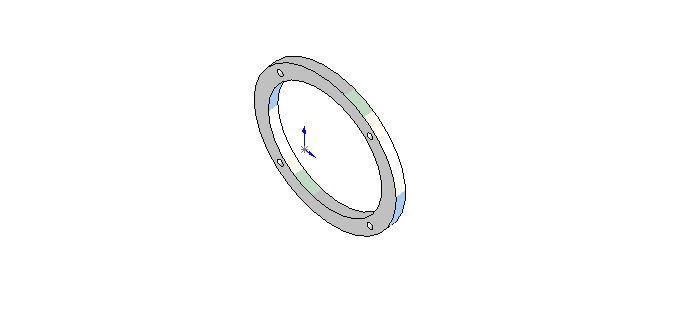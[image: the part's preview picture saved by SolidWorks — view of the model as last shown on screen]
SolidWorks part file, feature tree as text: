
SOLIDWORKS PART (.sldprt)
format: sldprt  version: not decoded by parser v0  size: 283,648 bytes
history: native  units: mm
features: sketch x4, plane x3, extrude x1 + 1 further entry (+7 scaffold rows collapsed)
feature tree (16):
  scaffold x7  (default folders/planes/origin — collapsed)
  "Corps de surface"
  plane  "Face"
  plane  "Dessus"
  plane  "Droite"
  sketch  "Esquisse1"  dims[c1.D1=4.8mm c1.D2=4.8mm c1.D7=4.8mm c1.D8=4.8mm c1.D17=~42.860884mm c1.D18=~42.860884mm c1.D3=32.0mm c1.D4=4.8mm c1.D5=8.0mm c1.D6=8.0mm c2.D7=4.8mm c2.D4=4.0mm c2.D5=5.6mm c2.D6=48.0mm c2.D9=32.0mm c2.D10=4.0mm c2.D11=5.6mm c2.D12=48.0mm c2.D13=28.8mm c2.D14=8.0mm c2.D15=8.0mm c2.D16=16.0mm c2.D18=48.0mm c3.D16=16.0mm c3.D17=8.0mm c3.D18=8.0mm c3.D19=4.0mm c3.D20=4.0mm c3.D21=24.0mm c3.D22=25.0mm c3.D13=28.8mm c3.D3=64.0mm c3.D12=8.0mm c4.D17=8.0mm c4.D9=8.0mm c4.D12=64.0mm c5.D17=48.0mm c5.D18=8.0mm c5.D9=32.0mm c6.D17=16.0mm c6.D18=16.0mm]
  sketch  "Esquisse5"  dims[c1.D12=2.1mm c1.D16=2.1mm c1.D1=8.0mm c1.D2=8.0mm c1.D3=4.0mm c1.D4=4.0mm c1.D5=25.0mm c1.D6=24.0mm c1.D7=12.5mm c1.D8=9.6mm c1.D9=5.5mm c1.D10=20.8mm c1.D11=10.4mm c1.D13=9.5mm c1.D14=2.0mm c1.D15=12.5mm c2.D16=~5.972653mm]
  sketch  "Esquisse6"  dims[D1=75.0mm D5=5.0mm D6=5.0mm D7=5.0mm D8=5.0mm D9=2.1mm D10=2.1mm D11=2.1mm D12=2.1mm D2=2.5mm D3=2.5mm D4=2.0mm]
  sketch  "Esquisse7"  dims[c1.D1=75.0mm c1.D2=60.0mm c1.D3=3.1mm c1.D4=33.5mm c1.D5=33.5mm c2.D5=45.0deg c2.D6=~23.688077mm]
  extrude  "Extrusion2"  Depth=5mm
decode coverage: 5 of 5 modeling features carry decoded parameters; 1 rows unclassified (native names shown)
note: ~ marks probable driven/reference dimensions
note: suppression state not decoded; provenance and decode notes live in map.json
